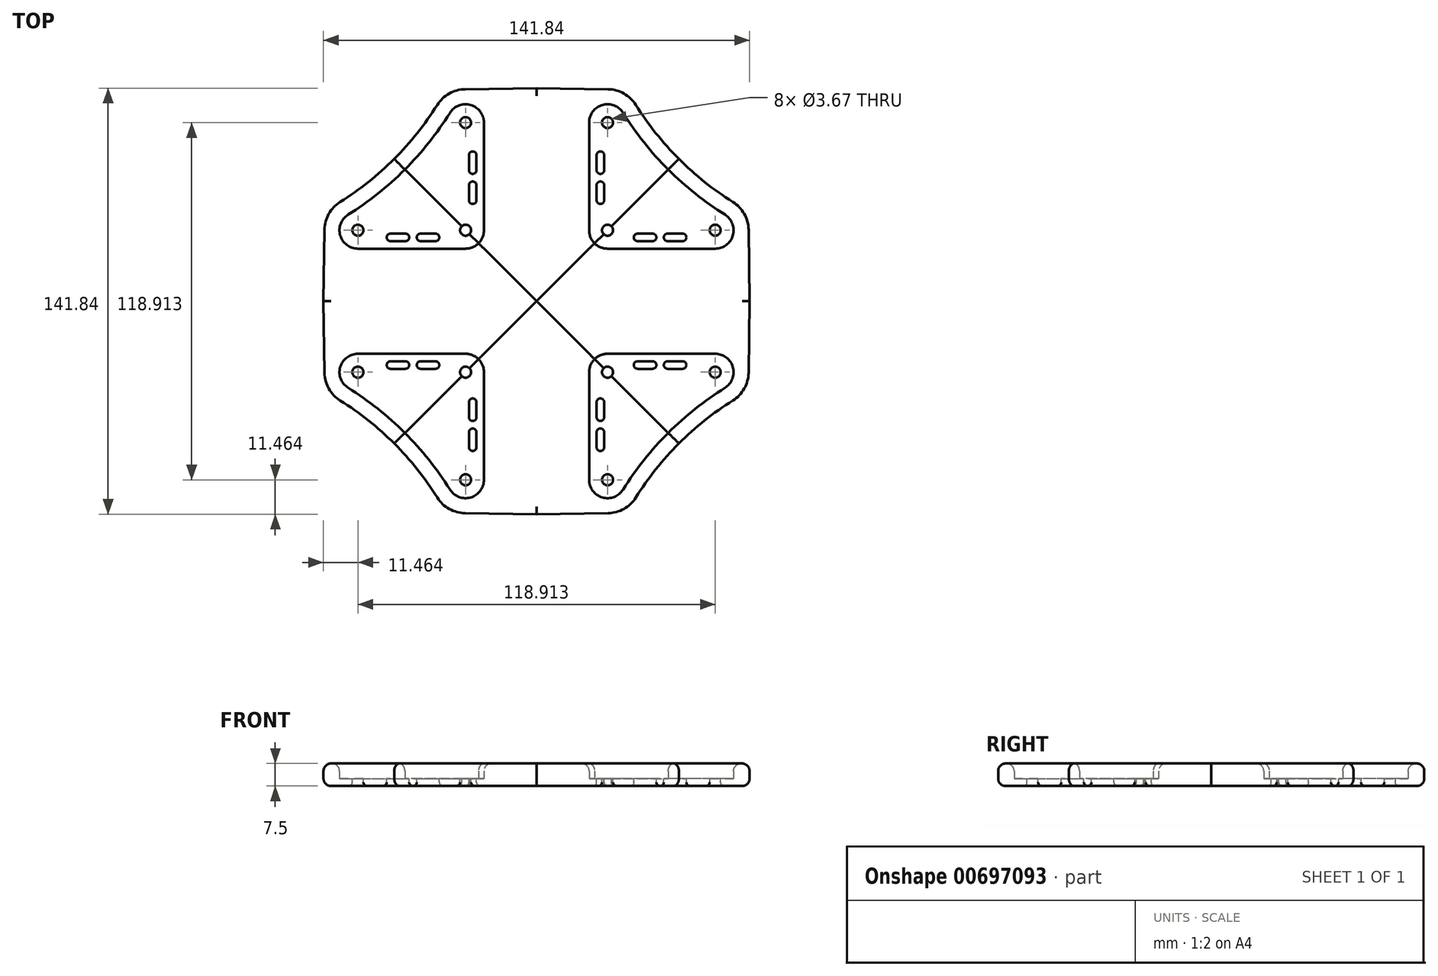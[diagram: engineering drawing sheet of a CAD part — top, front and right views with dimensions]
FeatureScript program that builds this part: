
annotation { "Feature Type Name" : "Feature", "Feature Type Description" : "" }
export const myFeature = defineFeature(function(context is Context, id is Id, definition is map)
    precondition{}
    {
        {
            var Q0;
            Q0=qCreatedBy(makeId("Top.planeOp"),FACE);
            var sketch = newSketch(context, id + "F0", { "sketchPlane" : qUnion([Q0])});
            skArc(sketch, "E0.0", {"start": v(-62.7, 28.82) * mm, "mid": v(-52.85, 35.8) * mm, "end": v(-43.84, 43.84) * mm});
            skLineSegment(sketch, "E1", {"start": v(-59.46, 17.5) * mm, "end": v(-23.63, 17.5) * mm});
            skPoint(sketch, "E2.visualSharp", {"position": v(-151.83, 17.5) * mm});
            skArc(sketch, "E2.filletArc", {"start": v(-62.7, 28.82) * mm, "mid": v(-65.34, 21.93) * mm, "end": v(-59.46, 17.5) * mm});
            skArc(sketch, "E3", {"start": v(-23.63, 17.5) * mm, "mid": v(-21.28, 17.97) * mm, "end": v(-19.3, 19.3) * mm});
            skPoint(sketch, "E4.endSnap0", {"position": v(-63.5, 0) * mm});
            skLineSegment(sketch, "E5.0", {"start": v(0, 0) * mm, "end": v(-70.92, 0) * mm});
            skLineSegment(sketch, "E6.0", {"start": v(0, 0) * mm, "end": v(-19.3, 19.3) * mm});
            skArc(sketch, "E7.0", {"start": v(-65.36, 33.05) * mm, "mid": v(-55.96, 39.7) * mm, "end": v(-47.38, 47.38) * mm});
            skLineSegment(sketch, "E8.trimOffspring", {"start": v(-43.84, 43.84) * mm, "end": v(-47.38, 47.38) * mm});
            skLineSegment(sketch, "E9", {"start": v(-59.46, 17.5) * mm, "end": v(-59.46, 0) * mm, "construction": true});
            skArc(sketch, "E10", {"start": v(-65.36, 33.05) * mm, "mid": v(-69.15, 29.08) * mm, "end": v(-70.58, 23.78) * mm});
            skLineSegment(sketch, "E11", {"start": v(-70.58, 23.78) * mm, "end": v(-70.92, 0) * mm});
            skSolve(sketch);
        }
        {
            var Q0;
            Q0=makeQuery(id+"F0.imprint","IMPRINT",FACE,{"disambiguationData":[TD([[makeQuery(id+"F0.imprint","IMPRINT",EDGE,{"derivedFrom":sQuery(id+"F0.wireOp",EDGE,"E0.0")}),1.0]])]});
            extrude(context, id + "F1", {"entities" : qUnion([Q0]), "depth" : 5 * mm, "offsetDistance" : 25 * mm});
        }
        {
            var Q0;
            Q0=makeQuery(id+"F1.opExtrude","CAP_FACE",FACE,{"disambiguationData":[OSD([sQuery(id+"F0.wireOp",EDGE,"E0.0"),sQuery(id+"F0.wireOp",EDGE,"E1"),sQuery(id+"F0.wireOp",EDGE,"E2.filletArc"),sQuery(id+"F0.wireOp",EDGE,"E3"),sQuery(id+"F0.wireOp",EDGE,"E5.0"),sQuery(id+"F0.wireOp",EDGE,"E6.0"),sQuery(id+"F0.wireOp",EDGE,"E7.0"),sQuery(id+"F0.wireOp",EDGE,"E8.trimOffspring"),sQuery(id+"F0.wireOp",EDGE,"E10"),sQuery(id+"F0.wireOp",EDGE,"E11")])],"isStart":true});
            var sketch = newSketch(context, id + "F2", { "sketchPlane" : qUnion([Q0])});
            skLineSegment(sketch, "E12.0.3", {"start": v(-19.3, -19.3) * mm, "end": v(0, 0) * mm});
            skLineSegment(sketch, "E12.0.4", {"start": v(0, 0) * mm, "end": v(-70.92, 0) * mm});
            skLineSegment(sketch, "E12.0.5", {"start": v(-70.92, 0) * mm, "end": v(-70.58, -23.78) * mm});
            skArc(sketch, "E12.0.6", {"start": v(-70.58, -23.78) * mm, "mid": v(-69.15, -29.08) * mm, "end": v(-65.36, -33.05) * mm});
            skArc(sketch, "E12.0.7", {"start": v(-65.36, -33.05) * mm, "mid": v(-55.96, -39.7) * mm, "end": v(-47.38, -47.38) * mm});
            skLineSegment(sketch, "E12.0.8", {"start": v(-47.38, -47.38) * mm, "end": v(-43.84, -43.84) * mm});
            skLineSegment(sketch, "E13", {"start": v(-43.84, -43.84) * mm, "end": v(-19.3, -19.3) * mm});
            skSolve(sketch);
        }
        {
            var Q0;
            Q0 = qSketchRegion(id + "F2", true);
            extrude(context, id + "F3", {"entities" : qUnion([Q0]), "operationType" : NewBodyOperationType.ADD, "depth" : 2.5 * mm, "offsetDistance" : 25 * mm});
        }
        {
            var Q0;
            Q0=makeQuery(id+"F3.opExtrude","CAP_FACE",FACE,{"disambiguationData":[OSD([sQuery(id+"F2.wireOp",EDGE,"E12.0.3"),sQuery(id+"F2.wireOp",EDGE,"E12.0.4"),sQuery(id+"F2.wireOp",EDGE,"E12.0.5"),sQuery(id+"F2.wireOp",EDGE,"E12.0.6"),sQuery(id+"F2.wireOp",EDGE,"E12.0.7"),sQuery(id+"F2.wireOp",EDGE,"E12.0.8"),sQuery(id+"F2.wireOp",EDGE,"E13")])],"isStart":true});
            var sketch = newSketch(context, id + "F4", { "sketchPlane" : qUnion([Q0])});
            skPoint(sketch, "E14.orphan", {"position": v(-41.62, 41.62) * mm});
            skCircle(sketch, "E15", {"center": v(-59.46, 23.63) * mm, "radius": 3.63 * mm, "construction": true});
            skLineSegment(sketch, "E16", {"start": v(-59.46, 20) * mm, "end": v(-59.46, 21.79) * mm, "construction": true});
            skCircle(sketch, "E17", {"center": v(-59.46, 23.63) * mm, "radius": 1.84 * mm});
            skCircle(sketch, "E18", {"center": v(-23.63, 23.63) * mm, "radius": 1.84 * mm});
            skArc(sketch, "E19.1.0.0", {"start": v(-38.63, 22.5) * mm, "mid": v(-39.88, 21.25) * mm, "end": v(-38.63, 20) * mm});
            skLineSegment(sketch, "E19.1.0.1", {"start": v(-38.63, 22.5) * mm, "end": v(-33.63, 22.5) * mm});
            skArc(sketch, "E19.1.0.2", {"start": v(-33.63, 20) * mm, "mid": v(-32.38, 21.25) * mm, "end": v(-33.63, 22.5) * mm});
            skLineSegment(sketch, "E19.1.0.3", {"start": v(-33.63, 20) * mm, "end": v(-38.63, 20) * mm});
            skArc(sketch, "E19.2.0.0", {"start": v(-48.63, 22.5) * mm, "mid": v(-49.88, 21.25) * mm, "end": v(-48.63, 20) * mm});
            skLineSegment(sketch, "E19.2.0.1", {"start": v(-48.63, 22.5) * mm, "end": v(-43.63, 22.5) * mm});
            skArc(sketch, "E19.2.0.2", {"start": v(-43.63, 20) * mm, "mid": v(-42.38, 21.25) * mm, "end": v(-43.63, 22.5) * mm});
            skLineSegment(sketch, "E19.2.0.3", {"start": v(-43.63, 20) * mm, "end": v(-48.63, 20) * mm});
            skLineSegment(sketch, "E19.direction1", {"start": v(-28.63, 20) * mm, "end": v(-38.63, 20) * mm, "construction": true});
            skSolve(sketch);
        }
        {
            var Q0;
            Q0 = qSketchRegion(id + "F4", true);
            extrude(context, id + "F5", {"entities" : qUnion([Q0]), "operationType" : NewBodyOperationType.REMOVE, "endBound" : BoundingType.THROUGH_ALL, "oppositeDirection" : true, "depth" : 25 * mm, "offsetDistance" : 25 * mm});
        }
        {
            var Q0;
            Q0=makeQuery(id+"F1.opExtrude","CAP_EDGE",EDGE,{"disambiguationData":[OSD([sQuery(id+"F0.wireOp",EDGE,"E0.0")])],"isStart":true});
            var Q1;
            Q1=makeQuery(id+"F1.opExtrude","CAP_EDGE",EDGE,{"disambiguationData":[OSD([sQuery(id+"F0.wireOp",EDGE,"E0.0")])],"isStart":false});
            var Q2;
            Q2=makeQuery(id+"F1.opExtrude","CAP_EDGE",EDGE,{"disambiguationData":[OSD([sQuery(id+"F0.wireOp",EDGE,"E7.0")])],"isStart":false});
            var Q3;
            Q3=makeQuery(id+"F3.opExtrude","CAP_EDGE",EDGE,{"disambiguationData":[OSD([sQuery(id+"F2.wireOp",EDGE,"E12.0.7")])],"isStart":false});
            fillet(context, id + "F6", {"entities" : qUnion([Q0, Q1, Q2, Q3]), "tangentPropagation" : true, "radius" : 2.5 * mm, "defaultsChanged" : false, "vertexSettings" : [], "allowEdgeOverflow" : false});
        }
        {
            var Q0;
            Q0=makeQuery(id+"F5.boolean.opBoolean","COPY",EDGE,{"derivedFrom":makeQuery(id+"F5.opExtrude","CAP_EDGE",EDGE,{"disambiguationData":[OSD([sQuery(id+"F4.wireOp",EDGE,"E17")])],"isStart":true})});
            var Q1;
            Q1=makeQuery(id+"F5.boolean.opBoolean","COPY",EDGE,{"derivedFrom":makeQuery(id+"F5.opExtrude","CAP_EDGE",EDGE,{"disambiguationData":[OSD([sQuery(id+"F4.wireOp",EDGE,"E18")])],"isStart":true})});
            var Q2;
            Q2=makeQuery(id+"F5.boolean.opBoolean","INTERSECT",EDGE,{"derivedFrom":[makeQuery(id+"F3.opExtrude","CAP_FACE",FACE,{"disambiguationData":[OSD([sQuery(id+"F2.wireOp",EDGE,"E12.0.3"),sQuery(id+"F2.wireOp",EDGE,"E12.0.4"),sQuery(id+"F2.wireOp",EDGE,"E12.0.5"),sQuery(id+"F2.wireOp",EDGE,"E12.0.6"),sQuery(id+"F2.wireOp",EDGE,"E12.0.7"),sQuery(id+"F2.wireOp",EDGE,"E12.0.8"),sQuery(id+"F2.wireOp",EDGE,"E13")])],"isStart":false}),makeQuery(id+"F5.opExtrude","SWEPT_FACE",FACE,{"disambiguationData":[OSD([sQuery(id+"F4.wireOp",EDGE,"E18")])]})]});
            var Q3;
            Q3=makeQuery(id+"F5.boolean.opBoolean","INTERSECT",EDGE,{"derivedFrom":[makeQuery(id+"F3.opExtrude","CAP_FACE",FACE,{"disambiguationData":[OSD([sQuery(id+"F2.wireOp",EDGE,"E12.0.3"),sQuery(id+"F2.wireOp",EDGE,"E12.0.4"),sQuery(id+"F2.wireOp",EDGE,"E12.0.5"),sQuery(id+"F2.wireOp",EDGE,"E12.0.6"),sQuery(id+"F2.wireOp",EDGE,"E12.0.7"),sQuery(id+"F2.wireOp",EDGE,"E12.0.8"),sQuery(id+"F2.wireOp",EDGE,"E13")])],"isStart":false}),makeQuery(id+"F5.opExtrude","SWEPT_FACE",FACE,{"disambiguationData":[OSD([sQuery(id+"F4.wireOp",EDGE,"E17")])]})]});
            var Q4;
            Q4=makeQuery(id+"F5.boolean.opBoolean","INTERSECT",EDGE,{"derivedFrom":[makeQuery(id+"F3.opExtrude","CAP_FACE",FACE,{"disambiguationData":[OSD([sQuery(id+"F2.wireOp",EDGE,"E12.0.3"),sQuery(id+"F2.wireOp",EDGE,"E12.0.4"),sQuery(id+"F2.wireOp",EDGE,"E12.0.5"),sQuery(id+"F2.wireOp",EDGE,"E12.0.6"),sQuery(id+"F2.wireOp",EDGE,"E12.0.7"),sQuery(id+"F2.wireOp",EDGE,"E12.0.8"),sQuery(id+"F2.wireOp",EDGE,"E13")])],"isStart":false}),makeQuery(id+"F5.opExtrude","SWEPT_FACE",FACE,{"disambiguationData":[OSD([sQuery(id+"F4.wireOp",EDGE,"E19.2.0.3")])]})]});
            var Q5;
            Q5=makeQuery(id+"F5.boolean.opBoolean","INTERSECT",EDGE,{"derivedFrom":[makeQuery(id+"F3.opExtrude","CAP_FACE",FACE,{"disambiguationData":[OSD([sQuery(id+"F2.wireOp",EDGE,"E12.0.3"),sQuery(id+"F2.wireOp",EDGE,"E12.0.4"),sQuery(id+"F2.wireOp",EDGE,"E12.0.5"),sQuery(id+"F2.wireOp",EDGE,"E12.0.6"),sQuery(id+"F2.wireOp",EDGE,"E12.0.7"),sQuery(id+"F2.wireOp",EDGE,"E12.0.8"),sQuery(id+"F2.wireOp",EDGE,"E13")])],"isStart":false}),makeQuery(id+"F5.opExtrude","SWEPT_FACE",FACE,{"disambiguationData":[OSD([sQuery(id+"F4.wireOp",EDGE,"E19.1.0.3")])]})]});
            var Q6;
            Q6=makeQuery(id+"F6.opFillet","BLEND_EDGE",EDGE,{"blendedFrom":[makeQuery(id+"F1.opExtrude","CAP_EDGE",EDGE,{"disambiguationData":[OSD([sQuery(id+"F0.wireOp",EDGE,"E1")])],"isStart":true}),makeQuery(id+"F5.boolean.opBoolean","COPY",FACE,{"derivedFrom":makeQuery(id+"F5.opExtrude","SWEPT_FACE",FACE,{"disambiguationData":[OSD([sQuery(id+"F4.wireOp",EDGE,"E19.2.0.3")])]})})],"blendedInto":[makeQuery(id+"F5.boolean.opBoolean","COPY",FACE,{"derivedFrom":makeQuery(id+"F5.opExtrude","SWEPT_FACE",FACE,{"disambiguationData":[OSD([sQuery(id+"F4.wireOp",EDGE,"E19.2.0.3")])]})})]});
            var Q7;
            Q7=makeQuery(id+"F6.opFillet","BLEND_EDGE",EDGE,{"blendedFrom":[makeQuery(id+"F1.opExtrude","CAP_EDGE",EDGE,{"disambiguationData":[OSD([sQuery(id+"F0.wireOp",EDGE,"E1")])],"isStart":true}),makeQuery(id+"F5.boolean.opBoolean","COPY",FACE,{"derivedFrom":makeQuery(id+"F5.opExtrude","SWEPT_FACE",FACE,{"disambiguationData":[OSD([sQuery(id+"F4.wireOp",EDGE,"E19.1.0.3")])]})})],"blendedInto":[makeQuery(id+"F5.boolean.opBoolean","COPY",FACE,{"derivedFrom":makeQuery(id+"F5.opExtrude","SWEPT_FACE",FACE,{"disambiguationData":[OSD([sQuery(id+"F4.wireOp",EDGE,"E19.1.0.3")])]})})]});
            fillet(context, id + "F7", {"entities" : qUnion([Q0, Q1, Q2, Q3, Q4, Q5, Q6, Q7]), "tangentPropagation" : true, "radius" : 1.25 * mm, "defaultsChanged" : false, "vertexSettings" : [], "allowEdgeOverflow" : false});
        }
        {
            var Q0;
            Q0=makeQuery(id+"F1.opExtrude","SWEPT_BODY",BODY,{"disambiguationData":[OSD([sQuery(id+"F0.wireOp",EDGE,"E0.0"),sQuery(id+"F0.wireOp",EDGE,"E1"),sQuery(id+"F0.wireOp",EDGE,"E2.filletArc"),sQuery(id+"F0.wireOp",EDGE,"E3"),sQuery(id+"F0.wireOp",EDGE,"E5.0"),sQuery(id+"F0.wireOp",EDGE,"E6.0"),sQuery(id+"F0.wireOp",EDGE,"E7.0"),sQuery(id+"F0.wireOp",EDGE,"E8.trimOffspring"),sQuery(id+"F0.wireOp",EDGE,"E10"),sQuery(id+"F0.wireOp",EDGE,"E11")])]});
            var Q1;
            Q1=makeQuery(id+"F3.boolean.opBoolean","MERGE",FACE,{"derivedFrom":[makeQuery(id+"F1.opExtrude","SWEPT_FACE",FACE,{"disambiguationData":[OSD([sQuery(id+"F0.wireOp",EDGE,"E5.0")])]}),makeQuery(id+"F3.opExtrude","SWEPT_FACE",FACE,{"disambiguationData":[OSD([sQuery(id+"F2.wireOp",EDGE,"E12.0.4")])]})]});
            mirror(context, id + "F8", {"operationType" : NewBodyOperationType.ADD, "entities" : qUnion([Q0]), "mirrorPlane" : qUnion([Q1])});
        }
        {
            var Q0;
            Q0=makeQuery(id+"F1.opExtrude","SWEPT_BODY",BODY,{"disambiguationData":[OSD([sQuery(id+"F0.wireOp",EDGE,"E0.0"),sQuery(id+"F0.wireOp",EDGE,"E1"),sQuery(id+"F0.wireOp",EDGE,"E2.filletArc"),sQuery(id+"F0.wireOp",EDGE,"E3"),sQuery(id+"F0.wireOp",EDGE,"E5.0"),sQuery(id+"F0.wireOp",EDGE,"E6.0"),sQuery(id+"F0.wireOp",EDGE,"E7.0"),sQuery(id+"F0.wireOp",EDGE,"E8.trimOffspring"),sQuery(id+"F0.wireOp",EDGE,"E10"),sQuery(id+"F0.wireOp",EDGE,"E11")])]});
            var Q1;
            {var subQ0=makeQuery(id+"F3.boolean.opBoolean","MERGE",EDGE,{"derivedFrom":[makeQuery(id+"F1.opExtrude","SWEPT_EDGE",EDGE,{"disambiguationData":[OSD([sQuery(id+"F0.wireOp",EDGE,"E5.0"),sQuery(id+"F0.wireOp",EDGE,"E6.0")])]}),makeQuery(id+"F3.opExtrude","SWEPT_EDGE",EDGE,{"disambiguationData":[OSD([sQuery(id+"F2.wireOp",EDGE,"E12.0.3"),sQuery(id+"F2.wireOp",EDGE,"E12.0.4")])]})]});Q1=makeQuery(id+"F8.boolean.opBoolean","MERGE",EDGE,{"derivedFrom":[subQ0,makeQuery(id+"F8.opPattern","COPY",EDGE,{"derivedFrom":subQ0,"instanceName":"1"})]});}
            circularPattern(context, id + "F9", {"entities" : qUnion([Q0]), "axis" : qUnion([Q1]), "angle" : 360 * degree, "instanceCount" : 4, "equalSpace" : true});
        }
    });
